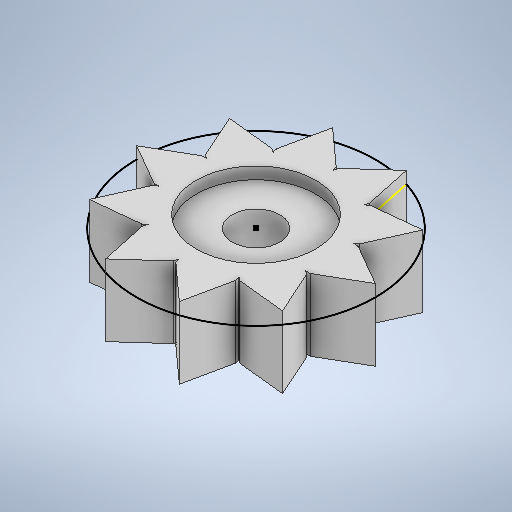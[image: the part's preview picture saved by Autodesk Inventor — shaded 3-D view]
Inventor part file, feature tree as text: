
AUTODESK INVENTOR PART (.ipt)
format: ipt  version: 2025.2 (Build 292293000, 293)  size: 310,784 bytes
history: native  units: mm
features: sketch x3, extrude x2, pattern_circular x1
ambient origin geometry x8: Origin, YZ Plane, XZ Plane, XY Plane, X Axis, Y Axis, Z Axis, Center Point
bodies: Solid1 (feature_tree)
feature tree (6):
  extrude  "Extrusion1"  Depth=45.0mm
  extrude  "Extrusion4"  Depth=20.0mm
  pattern_circular  "Circular Pattern2"  Count=2  [1 undecoded]
  sketch  "Sketch6"  dims[d5=5.0mm d6=5.0mm d7=5.0mm d8=5.0mm d9=2.0mm d10=0.0mm d27=10.0mm d28=5.0mm d29=2.0mm d30=10.0mm d31=2.0mm d32=30.0deg d33=2.0mm d34=30.0deg d35=0.5mm d36=2.5mm d37=0.0mm d38=0.0mm d39=100.0mm d40=360.0deg]
  sketch  "Sketch1"  dims[d0=50.0mm d1=45.0mm]
  sketch  "Sketch5"  dims[d2=4.5mm d3=20.0mm d4=20.0mm]
note: 1 required parameter value undecoded (feature->parameter linkage not recoverable at this tier; creation-order binding heuristic only, values carry confidence <= 0.55)
